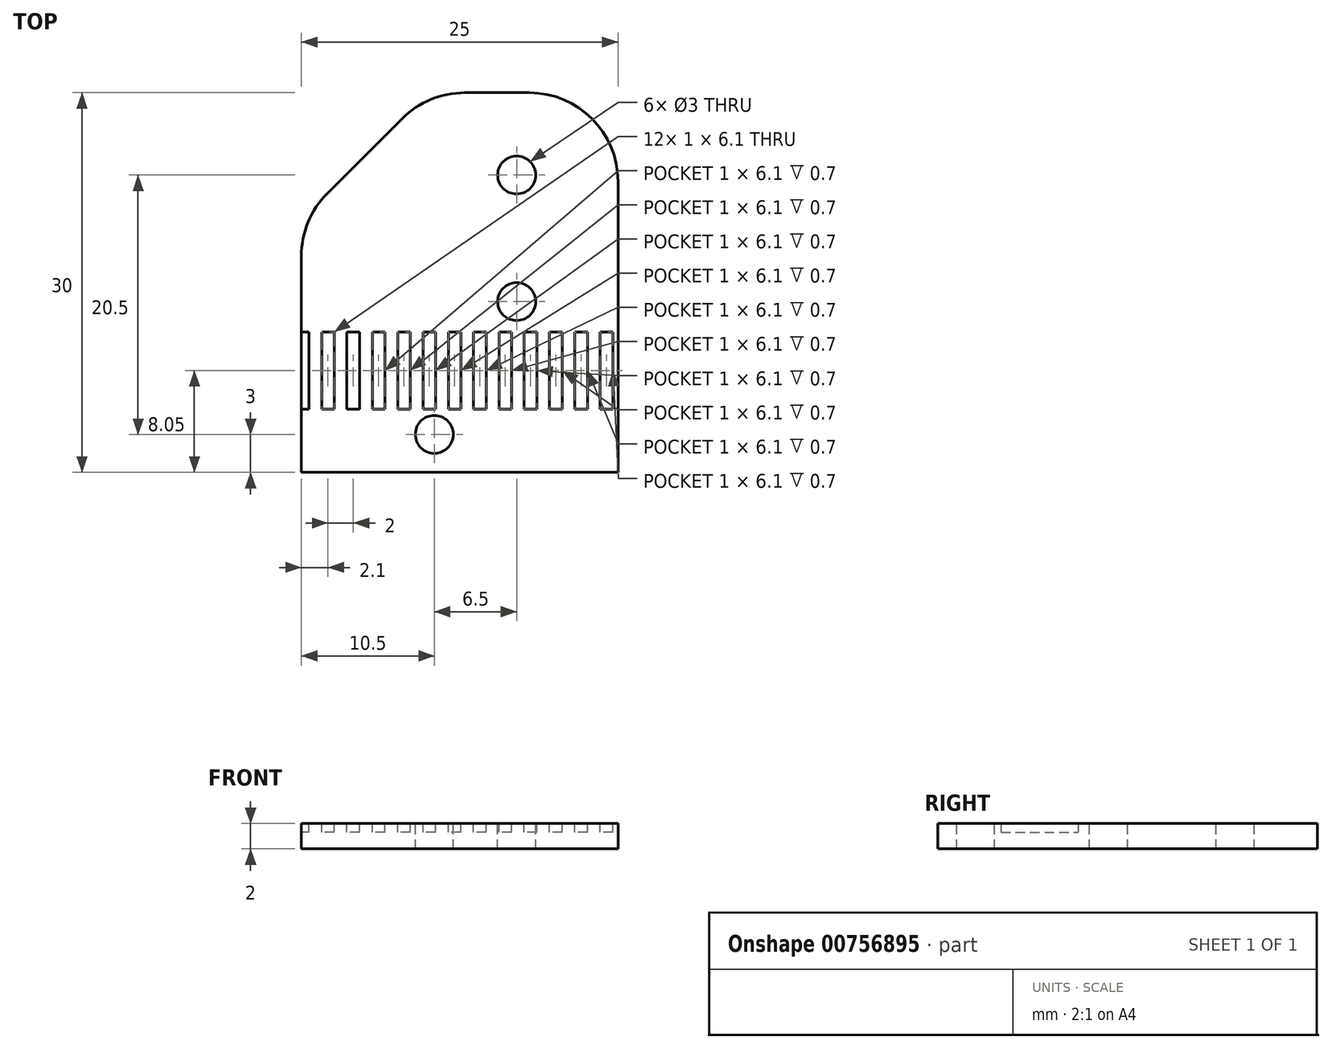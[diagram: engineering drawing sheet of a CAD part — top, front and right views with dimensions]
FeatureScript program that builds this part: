
annotation { "Feature Type Name" : "Feature", "Feature Type Description" : "" }
export const myFeature = defineFeature(function(context is Context, id is Id, definition is map)
    precondition{}
    {
        {
            var Q0;
            Q0=qCreatedBy(makeId("Top.planeOp"),FACE);
            var sketch = newSketch(context, id + "F0", { "sketchPlane" : qUnion([Q0])});
            skLineSegment(sketch, "E0.bottom", {"start": v(12.5, -15) * mm, "end": v(-12.5, -15) * mm});
            skLineSegment(sketch, "E0.top", {"start": v(12.5, 15) * mm, "end": v(-12.5, 15) * mm});
            skLineSegment(sketch, "E0.left", {"start": v(12.5, -15) * mm, "end": v(12.5, 15) * mm});
            skLineSegment(sketch, "E0.right", {"start": v(-12.5, -15) * mm, "end": v(-12.5, 15) * mm});
            skPoint(sketch, "E0.middle", {"position": v(0, 0) * mm});
            skSolve(sketch);
        }
        {
            var Q0;
            Q0=makeQuery(id+"F0.imprint","IMPRINT",FACE,{"disambiguationData":[TD([[makeQuery(id+"F0.imprint","IMPRINT",EDGE,{"derivedFrom":sQuery(id+"F0.wireOp",EDGE,"E0.bottom")}),-1.0]])]});
            extrude(context, id + "F1", {"entities" : qUnion([Q0]), "depth" : 2 * mm, "offsetDistance" : 25 * mm});
        }
        {
            var Q0;
            Q0=makeQuery(id+"F1.opExtrude","CAP_FACE",FACE,{"disambiguationData":[OSD([sQuery(id+"F0.wireOp",EDGE,"E0.bottom"),sQuery(id+"F0.wireOp",EDGE,"E0.top"),sQuery(id+"F0.wireOp",EDGE,"E0.left"),sQuery(id+"F0.wireOp",EDGE,"E0.right")])],"isStart":false});
            var sketch = newSketch(context, id + "F2", { "sketchPlane" : qUnion([Q0])});
            skCircle(sketch, "E1", {"center": v(-2, -12) * mm, "radius": 1.5 * mm});
            skPoint(sketch, "E1.centerSnap0", {"position": v(0, -15) * mm});
            skCircle(sketch, "E2", {"center": v(4.5, -1.5) * mm, "radius": 1.5 * mm});
            skCircle(sketch, "E3", {"center": v(4.5, 8.5) * mm, "radius": 1.5 * mm});
            skSolve(sketch);
        }
        {
            var Q0;
            Q0 = qSketchRegion(id + "F2", true);
            extrude(context, id + "F3", {"entities" : qUnion([Q0]), "operationType" : NewBodyOperationType.REMOVE, "endBound" : BoundingType.THROUGH_ALL, "oppositeDirection" : true, "depth" : 25 * mm, "offsetDistance" : 25 * mm});
        }
        {
            var Q0;
            Q0=makeQuery(id+"F1.opExtrude","CAP_FACE",FACE,{"disambiguationData":[OSD([sQuery(id+"F0.wireOp",EDGE,"E0.bottom"),sQuery(id+"F0.wireOp",EDGE,"E0.top"),sQuery(id+"F0.wireOp",EDGE,"E0.left"),sQuery(id+"F0.wireOp",EDGE,"E0.right")])],"isStart":false});
            var sketch = newSketch(context, id + "F4", { "sketchPlane" : qUnion([Q0])});
            skLineSegment(sketch, "E4.bottom", {"start": v(12.1, -10) * mm, "end": v(11.1, -10) * mm});
            skLineSegment(sketch, "E4.top", {"start": v(12.1, -3.9) * mm, "end": v(11.1, -3.9) * mm});
            skLineSegment(sketch, "E4.left", {"start": v(12.1, -10) * mm, "end": v(12.1, -3.9) * mm});
            skLineSegment(sketch, "E4.right", {"start": v(11.1, -10) * mm, "end": v(11.1, -3.9) * mm});
            skPoint(sketch, "E4.middle", {"position": v(11.6, -6.95) * mm});
            skLineSegment(sketch, "E5.bottom", {"start": v(10.1, -10) * mm, "end": v(9.1, -10) * mm});
            skLineSegment(sketch, "E5.top", {"start": v(10.1, -3.9) * mm, "end": v(9.1, -3.9) * mm});
            skLineSegment(sketch, "E5.left", {"start": v(10.1, -10) * mm, "end": v(10.1, -3.9) * mm});
            skLineSegment(sketch, "E5.right", {"start": v(9.1, -10) * mm, "end": v(9.1, -3.9) * mm});
            skPoint(sketch, "E5.middle", {"position": v(9.6, -6.95) * mm});
            skLineSegment(sketch, "E6.bottom", {"start": v(8.1, -10) * mm, "end": v(7.1, -10) * mm});
            skLineSegment(sketch, "E6.top", {"start": v(8.1, -3.9) * mm, "end": v(7.1, -3.9) * mm});
            skLineSegment(sketch, "E6.left", {"start": v(8.1, -10) * mm, "end": v(8.1, -3.9) * mm});
            skLineSegment(sketch, "E6.right", {"start": v(7.1, -10) * mm, "end": v(7.1, -3.9) * mm});
            skPoint(sketch, "E6.middle", {"position": v(7.6, -6.95) * mm});
            skLineSegment(sketch, "E7.bottom", {"start": v(6.1, -10) * mm, "end": v(5.1, -10) * mm});
            skLineSegment(sketch, "E7.top", {"start": v(6.1, -3.9) * mm, "end": v(5.1, -3.9) * mm});
            skLineSegment(sketch, "E7.left", {"start": v(6.1, -10) * mm, "end": v(6.1, -3.9) * mm});
            skLineSegment(sketch, "E7.right", {"start": v(5.1, -10) * mm, "end": v(5.1, -3.9) * mm});
            skPoint(sketch, "E7.middle", {"position": v(5.6, -6.95) * mm});
            skLineSegment(sketch, "E8.bottom", {"start": v(4.1, -10) * mm, "end": v(3.1, -10) * mm});
            skLineSegment(sketch, "E8.top", {"start": v(4.1, -3.9) * mm, "end": v(3.1, -3.9) * mm});
            skLineSegment(sketch, "E8.left", {"start": v(4.1, -10) * mm, "end": v(4.1, -3.9) * mm});
            skLineSegment(sketch, "E8.right", {"start": v(3.1, -10) * mm, "end": v(3.1, -3.9) * mm});
            skPoint(sketch, "E8.middle", {"position": v(3.6, -6.95) * mm});
            skLineSegment(sketch, "E9.bottom", {"start": v(2.1, -10) * mm, "end": v(1.1, -10) * mm});
            skLineSegment(sketch, "E9.top", {"start": v(2.1, -3.9) * mm, "end": v(1.1, -3.9) * mm});
            skLineSegment(sketch, "E9.left", {"start": v(2.1, -10) * mm, "end": v(2.1, -3.9) * mm});
            skLineSegment(sketch, "E9.right", {"start": v(1.1, -10) * mm, "end": v(1.1, -3.9) * mm});
            skPoint(sketch, "E9.middle", {"position": v(1.6, -6.95) * mm});
            skLineSegment(sketch, "E10.bottom", {"start": v(0.1, -10) * mm, "end": v(-0.9, -10) * mm});
            skLineSegment(sketch, "E10.top", {"start": v(0.1, -3.9) * mm, "end": v(-0.9, -3.9) * mm});
            skLineSegment(sketch, "E10.left", {"start": v(0.1, -10) * mm, "end": v(0.1, -3.9) * mm});
            skLineSegment(sketch, "E10.right", {"start": v(-0.9, -10) * mm, "end": v(-0.9, -3.9) * mm});
            skPoint(sketch, "E10.middle", {"position": v(-0.4, -6.95) * mm});
            skLineSegment(sketch, "E11", {"start": v(-12.5, -10) * mm, "end": v(12.5, -10) * mm, "construction": true});
            skLineSegment(sketch, "E12", {"start": v(12.5, -3.9) * mm, "end": v(-12.5, -3.9) * mm, "construction": true});
            skLineSegment(sketch, "E13.bottom", {"start": v(-1.9, -10) * mm, "end": v(-2.9, -10) * mm});
            skLineSegment(sketch, "E13.top", {"start": v(-1.9, -3.9) * mm, "end": v(-2.9, -3.9) * mm});
            skLineSegment(sketch, "E13.left", {"start": v(-1.9, -10) * mm, "end": v(-1.9, -3.9) * mm});
            skLineSegment(sketch, "E13.right", {"start": v(-2.9, -10) * mm, "end": v(-2.9, -3.9) * mm});
            skLineSegment(sketch, "E14.bottom", {"start": v(-3.9, -10) * mm, "end": v(-4.9, -10) * mm});
            skLineSegment(sketch, "E14.top", {"start": v(-3.9, -3.9) * mm, "end": v(-4.9, -3.9) * mm});
            skLineSegment(sketch, "E14.left", {"start": v(-3.9, -10) * mm, "end": v(-3.9, -3.9) * mm});
            skLineSegment(sketch, "E14.right", {"start": v(-4.9, -10) * mm, "end": v(-4.9, -3.9) * mm});
            skLineSegment(sketch, "E15.bottom", {"start": v(-5.9, -3.9) * mm, "end": v(-6.9, -3.9) * mm});
            skLineSegment(sketch, "E15.top", {"start": v(-5.9, -10) * mm, "end": v(-6.9, -10) * mm});
            skLineSegment(sketch, "E15.left", {"start": v(-5.9, -3.9) * mm, "end": v(-5.9, -10) * mm});
            skLineSegment(sketch, "E15.right", {"start": v(-6.9, -3.9) * mm, "end": v(-6.9, -10) * mm});
            skLineSegment(sketch, "E16.bottom", {"start": v(-7.9, -10) * mm, "end": v(-8.9, -10) * mm});
            skLineSegment(sketch, "E16.top", {"start": v(-7.9, -3.9) * mm, "end": v(-8.9, -3.9) * mm});
            skLineSegment(sketch, "E16.left", {"start": v(-7.9, -10) * mm, "end": v(-7.9, -3.9) * mm});
            skLineSegment(sketch, "E16.right", {"start": v(-8.9, -10) * mm, "end": v(-8.9, -3.9) * mm});
            skLineSegment(sketch, "E17.bottom", {"start": v(-9.9, -3.9) * mm, "end": v(-10.9, -3.9) * mm});
            skLineSegment(sketch, "E17.top", {"start": v(-9.9, -10) * mm, "end": v(-10.9, -10) * mm});
            skLineSegment(sketch, "E17.left", {"start": v(-9.9, -3.9) * mm, "end": v(-9.9, -10) * mm});
            skLineSegment(sketch, "E17.right", {"start": v(-10.9, -3.9) * mm, "end": v(-10.9, -10) * mm});
            skLineSegment(sketch, "E18.bottom", {"start": v(-11.9, -10) * mm, "end": v(-12.9, -10) * mm});
            skLineSegment(sketch, "E18.top", {"start": v(-11.9, -3.9) * mm, "end": v(-12.9, -3.9) * mm});
            skLineSegment(sketch, "E18.left", {"start": v(-11.9, -10) * mm, "end": v(-11.9, -3.9) * mm});
            skLineSegment(sketch, "E18.right", {"start": v(-12.9, -10) * mm, "end": v(-12.9, -3.9) * mm});
            skSolve(sketch);
        }
        {
            var Q0;
            Q0 = qSketchRegion(id + "F4", true);
            extrude(context, id + "F5", {"entities" : qUnion([Q0]), "operationType" : NewBodyOperationType.REMOVE, "oppositeDirection" : true, "depth" : 0.7 * mm, "offsetDistance" : 25 * mm});
        }
        {
            var Q0;
            Q0=makeQuery(id+"F1.opExtrude","SWEPT_EDGE",EDGE,{"disambiguationData":[OSD([sQuery(id+"F0.wireOp",EDGE,"E0.top"),sQuery(id+"F0.wireOp",EDGE,"E0.right")])]});
            chamfer(context, id + "F6", {"entities" : qUnion([Q0]), "width" : 10 * mm, "tangentPropagation" : true});
        }
        {
            var Q0;
            {var subQ0=sQuery(id+"F0.wireOp",EDGE,"E0.right");Q0=makeQuery(id+"F6.opChamfer","BLEND_EDGE",EDGE,{"blendedFrom":[makeQuery(id+"F1.opExtrude","SWEPT_EDGE",EDGE,{"disambiguationData":[OSD([sQuery(id+"F0.wireOp",EDGE,"E0.top"),subQ0])]}),makeQuery(id+"F1.opExtrude","SWEPT_FACE",FACE,{"disambiguationData":[OSD([subQ0])]})],"blendedInto":[makeQuery(id+"F1.opExtrude","SWEPT_FACE",FACE,{"disambiguationData":[OSD([subQ0])]})]});}
            var Q1;
            {var subQ0=sQuery(id+"F0.wireOp",EDGE,"E0.top");Q1=makeQuery(id+"F6.opChamfer","BLEND_EDGE",EDGE,{"blendedFrom":[makeQuery(id+"F1.opExtrude","SWEPT_EDGE",EDGE,{"disambiguationData":[OSD([subQ0,sQuery(id+"F0.wireOp",EDGE,"E0.right")])]}),makeQuery(id+"F1.opExtrude","SWEPT_FACE",FACE,{"disambiguationData":[OSD([subQ0])]})],"blendedInto":[makeQuery(id+"F1.opExtrude","SWEPT_FACE",FACE,{"disambiguationData":[OSD([subQ0])]})]});}
            var Q2;
            Q2=makeQuery(id+"F1.opExtrude","SWEPT_EDGE",EDGE,{"disambiguationData":[OSD([sQuery(id+"F0.wireOp",EDGE,"E0.top"),sQuery(id+"F0.wireOp",EDGE,"E0.left")])]});
            fillet(context, id + "F7", {"entities" : qUnion([Q0, Q1, Q2]), "radius" : 7 * mm, "tangentPropagation" : true, "allowEdgeOverflow" : false});
        }
    });
